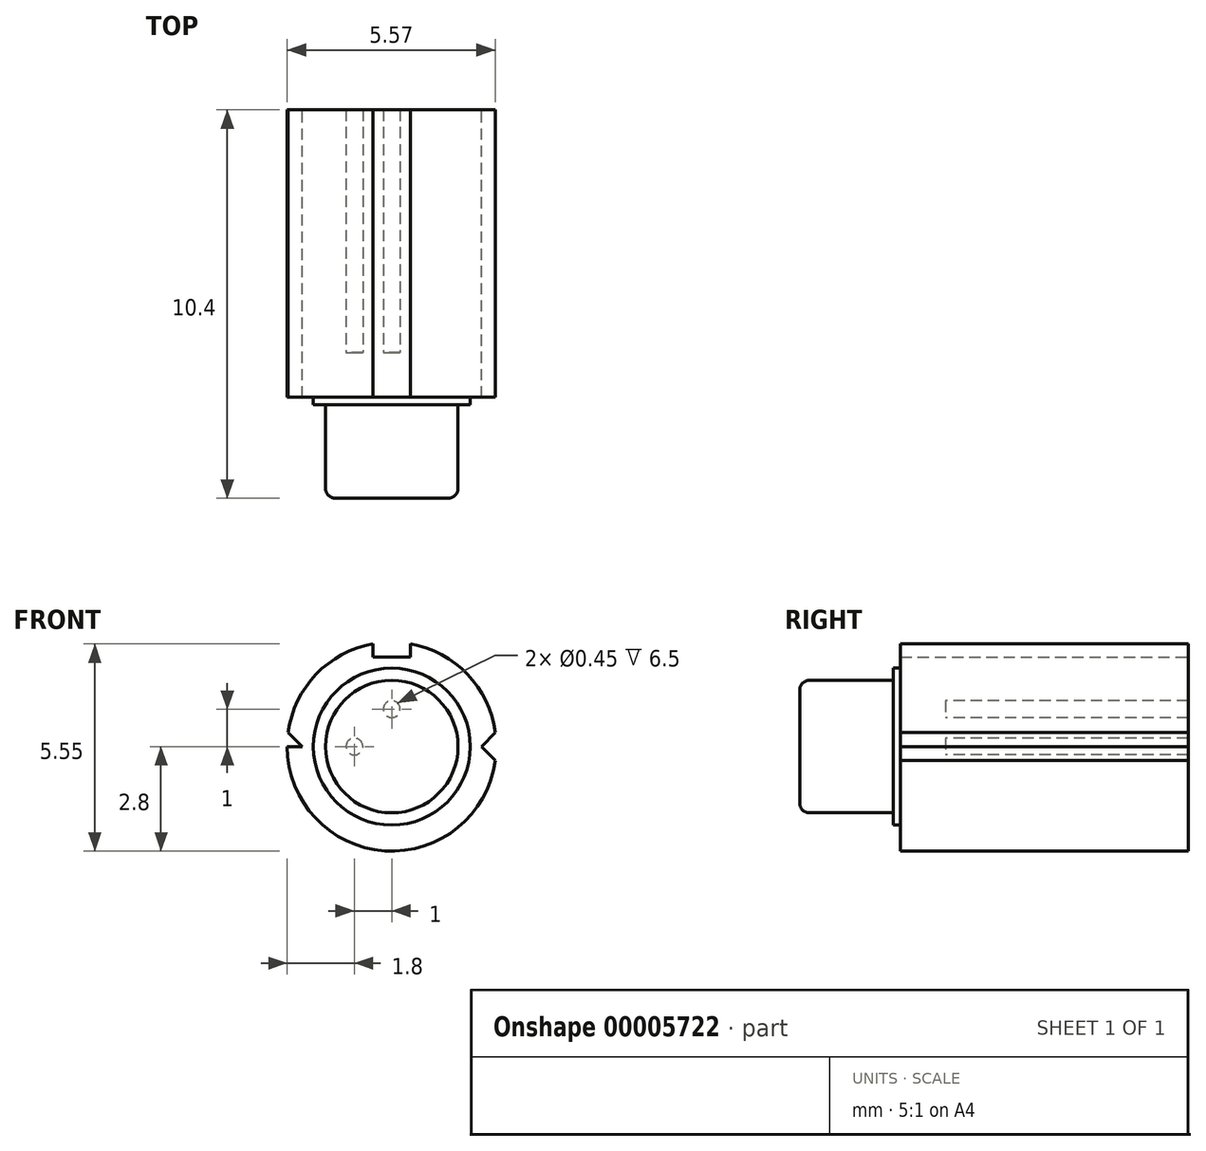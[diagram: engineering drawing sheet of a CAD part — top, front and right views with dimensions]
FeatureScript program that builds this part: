
annotation { "Feature Type Name" : "Feature", "Feature Type Description" : "" }
export const myFeature = defineFeature(function(context is Context, id is Id, definition is map)
    precondition{}
    {
        {
            var Q0;
            Q0=qCreatedBy(makeId("Front.planeOp"),FACE);
            var sketch = newSketch(context, id + "F0", { "sketchPlane" : qUnion([Q0])});
            skCircle(sketch, "E0", {"center": v(0, 0) * mm, "radius": 2.8 * mm});
            skSolve(sketch);
        }
        {
            var Q0;
            Q0=makeQuery(id+"F0.imprint","IMPRINT",FACE,{"disambiguationData":[TD([[makeQuery(id+"F0.imprint","IMPRINT",EDGE,{"derivedFrom":sQuery(id+"F0.wireOp",EDGE,"E0")}),1.0]])]});
            extrude(context, id + "F1", {"entities" : qUnion([Q0]), "depth" : 1.2 * mm});
        }
        {
            var Q0;
            Q0=makeQuery(id+"F1.opExtrude","CAP_FACE",FACE,{"disambiguationData":[OSD([sQuery(id+"F0.wireOp",EDGE,"E0")])],"isStart":false});
            var sketch = newSketch(context, id + "F2", { "sketchPlane" : qUnion([Q0])});
            skCircle(sketch, "E1", {"center": v(0, 0) * mm, "radius": 2.1 * mm});
            skSolve(sketch);
        }
        {
            var Q0;
            Q0=makeQuery(id+"F2.imprint","IMPRINT",FACE,{"disambiguationData":[TD([[makeQuery(id+"F2.imprint","IMPRINT",EDGE,{"derivedFrom":sQuery(id+"F2.wireOp",EDGE,"E1")}),1.0]])]});
            extrude(context, id + "F3", {"entities" : qUnion([Q0]), "operationType" : NewBodyOperationType.ADD, "depth" : 0.2 * mm});
        }
        {
            var Q0;
            Q0=makeQuery(id+"F3.opExtrude","CAP_FACE",FACE,{"disambiguationData":[OSD([sQuery(id+"F2.wireOp",EDGE,"E1")])],"isStart":false});
            var sketch = newSketch(context, id + "F4", { "sketchPlane" : qUnion([Q0])});
            skCircle(sketch, "E2", {"center": v(0, 0) * mm, "radius": 1.77 * mm});
            skSolve(sketch);
        }
        {
            var Q0;
            Q0=makeQuery(id+"F4.imprint","IMPRINT",FACE,{"disambiguationData":[TD([[makeQuery(id+"F4.imprint","IMPRINT",EDGE,{"derivedFrom":sQuery(id+"F4.wireOp",EDGE,"E2")}),1.0]])]});
            extrude(context, id + "F5", {"entities" : qUnion([Q0]), "operationType" : NewBodyOperationType.ADD, "depth" : 2.5 * mm});
        }
        {
            var Q0;
            Q0=makeQuery(id+"F5.opExtrude","CAP_EDGE",EDGE,{"disambiguationData":[OSD([sQuery(id+"F4.wireOp",EDGE,"E2")])],"isStart":false});
            fillet(context, id + "F6", {"entities" : qUnion([Q0]), "radius" : 0.27 * mm, "tangentPropagation" : true, "allowEdgeOverflow" : false});
        }
        {
            var Q0;
            Q0=makeQuery(id+"F1.opExtrude","CAP_FACE",FACE,{"disambiguationData":[OSD([sQuery(id+"F0.wireOp",EDGE,"E0")])],"isStart":true});
            var sketch = newSketch(context, id + "F7", { "sketchPlane" : qUnion([Q0])});
            skPoint(sketch, "E3", {"position": v(2.4, 0) * mm});
            skPoint(sketch, "E4", {"position": v(-2.4, 0) * mm});
            skLineSegment(sketch, "E5", {"start": v(2.4, 0) * mm, "end": v(2.77, -0.37) * mm});
            skLineSegment(sketch, "E6", {"start": v(2.77, -0.37) * mm, "end": v(2.4, 0) * mm});
            skLineSegment(sketch, "E7", {"start": v(2.4, 0) * mm, "end": v(2.77, 0.37) * mm});
            skLineSegment(sketch, "E8", {"start": v(2.8, 0) * mm, "end": v(-2.8, 0) * mm});
            skLineSegment(sketch, "E9", {"start": v(-2.4, 0) * mm, "end": v(-2.77, -0.37) * mm});
            skLineSegment(sketch, "E10", {"start": v(-2.4, 0) * mm, "end": v(-2.77, 0.37) * mm});
            skCircle(sketch, "E11", {"center": v(0, 0) * mm, "radius": 2.8 * mm});
            skPoint(sketch, "E12", {"position": v(0, 2.4) * mm});
            skLineSegment(sketch, "E13", {"start": v(0, 2.4) * mm, "end": v(0.5, 2.4) * mm});
            skLineSegment(sketch, "E14", {"start": v(0, 2.4) * mm, "end": v(-0.5, 2.4) * mm});
            skLineSegment(sketch, "E15", {"start": v(-0.5, 2.4) * mm, "end": v(-0.5, 2.75) * mm});
            skLineSegment(sketch, "E16", {"start": v(0.5, 2.4) * mm, "end": v(0.5, 2.75) * mm});
            skSolve(sketch);
        }
        {
            var Q0;
            {var subQ3=sQuery(id+"F7.wireOp",EDGE,"E7");Q0=makeQuery(id+"F7.imprint","IMPRINT",FACE,{"disambiguationData":[TD([[makeQuery(id+"F7.imprint","IMPRINT",EDGE,{"derivedFrom":subQ3}),-1.0]])]});}
            var Q1;
            {var subQ3=sQuery(id+"F7.wireOp",EDGE,"E6");Q1=makeQuery(id+"F7.imprint","IMPRINT",FACE,{"disambiguationData":[TD([[makeQuery(id+"F7.imprint","IMPRINT",EDGE,{"derivedFrom":subQ3}),-1.0]])]});}
            var Q2;
            {var subQ1=sQuery(id+"F7.wireOp",EDGE,"E9");Q2=makeQuery(id+"F7.imprint","IMPRINT",FACE,{"disambiguationData":[TD([[makeQuery(id+"F7.imprint","IMPRINT",EDGE,{"derivedFrom":subQ1}),-1.0]])]});}
            var Q3;
            {var subQ1=sQuery(id+"F7.wireOp",EDGE,"E10");Q3=makeQuery(id+"F7.imprint","IMPRINT",FACE,{"disambiguationData":[TD([[makeQuery(id+"F7.imprint","IMPRINT",EDGE,{"derivedFrom":subQ1}),1.0]])]});}
            var Q4;
            Q4=makeQuery(id+"F7.imprint","IMPRINT",FACE,{"disambiguationData":[TD([[makeQuery(id+"F7.imprint","IMPRINT",EDGE,{"derivedFrom":sQuery(id+"F7.wireOp",EDGE,"E13")}),1.0]])]});
            extrude(context, id + "F8", {"entities" : qUnion([Q0, Q1, Q2, Q3, Q4]), "operationType" : NewBodyOperationType.REMOVE, "endBound" : BoundingType.THROUGH_ALL, "oppositeDirection" : true, "depth" : 25 * mm});
        }
        {
            var Q0;
            Q0=makeQuery(id+"F1.opExtrude","CAP_FACE",FACE,{"disambiguationData":[OSD([sQuery(id+"F0.wireOp",EDGE,"E0")])],"isStart":true});
            var sketch = newSketch(context, id + "F9", { "sketchPlane" : qUnion([Q0])});
            skCircle(sketch, "E17", {"center": v(0, 0) * mm, "radius": 1 * mm});
            skPoint(sketch, "E18", {"position": v(0, 1) * mm});
            skPoint(sketch, "E19", {"position": v(-1, 0) * mm});
            skPoint(sketch, "E20", {"position": v(1, 0) * mm});
            skCircle(sketch, "E21", {"center": v(1, 0) * mm, "radius": 0.23 * mm});
            skCircle(sketch, "E22", {"center": v(0, 1) * mm, "radius": 0.23 * mm});
            skCircle(sketch, "E23", {"center": v(-1, 0) * mm, "radius": 0.23 * mm});
            skSolve(sketch);
        }
        {
            var Q0;
            {var subQ0=sQuery(id+"F9.wireOp",EDGE,"E22");var subQ1=sQuery(id+"F9.wireOp",EDGE,"E17");var subQ3=makeQuery(id+"F9.imprint","INTERSECT",VERTEX,{"disambiguationData":[OD(0.0)],"derivedFrom":[subQ1,subQ0]});Q0=makeQuery(id+"F9.imprint","IMPRINT",FACE,{"disambiguationData":[TD([[makeQuery(id+"F9.imprint","IMPRINT",EDGE,{"disambiguationData":[TD([[subQ3,-1.0]])],"derivedFrom":subQ1}),1.0]])]});}
            var Q1;
            {var subQ0=sQuery(id+"F9.wireOp",EDGE,"E22");var subQ1=sQuery(id+"F9.wireOp",EDGE,"E17");var subQ3=makeQuery(id+"F9.imprint","INTERSECT",VERTEX,{"disambiguationData":[OD(0.0)],"derivedFrom":[subQ1,subQ0]});Q1=makeQuery(id+"F9.imprint","IMPRINT",FACE,{"disambiguationData":[TD([[makeQuery(id+"F9.imprint","IMPRINT",EDGE,{"disambiguationData":[TD([[subQ3,-1.0]])],"derivedFrom":subQ1}),-1.0]])]});}
            var Q2;
            {var subQ0=sQuery(id+"F9.wireOp",EDGE,"E23");var subQ1=sQuery(id+"F9.wireOp",EDGE,"E17");var subQ3=makeQuery(id+"F9.imprint","INTERSECT",VERTEX,{"disambiguationData":[OD(0.0)],"derivedFrom":[subQ1,subQ0]});Q2=makeQuery(id+"F9.imprint","IMPRINT",FACE,{"disambiguationData":[TD([[makeQuery(id+"F9.imprint","IMPRINT",EDGE,{"disambiguationData":[TD([[subQ3,-1.0]])],"derivedFrom":subQ1}),1.0]])]});}
            var Q3;
            {var subQ0=sQuery(id+"F9.wireOp",EDGE,"E23");var subQ1=sQuery(id+"F9.wireOp",EDGE,"E17");var subQ3=makeQuery(id+"F9.imprint","INTERSECT",VERTEX,{"disambiguationData":[OD(0.0)],"derivedFrom":[subQ1,subQ0]});Q3=makeQuery(id+"F9.imprint","IMPRINT",FACE,{"disambiguationData":[TD([[makeQuery(id+"F9.imprint","IMPRINT",EDGE,{"disambiguationData":[TD([[subQ3,-1.0]])],"derivedFrom":subQ1}),-1.0]])]});}
            var Q4;
            {var subQ0=sQuery(id+"F9.wireOp",EDGE,"E21");var subQ1=sQuery(id+"F9.wireOp",EDGE,"E17");var subQ3=makeQuery(id+"F9.imprint","INTERSECT",VERTEX,{"disambiguationData":[OD(0.0)],"derivedFrom":[subQ1,subQ0]});Q4=makeQuery(id+"F9.imprint","IMPRINT",FACE,{"disambiguationData":[TD([[makeQuery(id+"F9.imprint","IMPRINT",EDGE,{"disambiguationData":[TD([[subQ3,1.0]])],"derivedFrom":subQ1}),1.0]])]});}
            var Q5;
            {var subQ0=sQuery(id+"F9.wireOp",EDGE,"E21");var subQ1=sQuery(id+"F9.wireOp",EDGE,"E17");var subQ3=makeQuery(id+"F9.imprint","INTERSECT",VERTEX,{"disambiguationData":[OD(0.0)],"derivedFrom":[subQ1,subQ0]});Q5=makeQuery(id+"F9.imprint","IMPRINT",FACE,{"disambiguationData":[TD([[makeQuery(id+"F9.imprint","IMPRINT",EDGE,{"disambiguationData":[TD([[subQ3,1.0]])],"derivedFrom":subQ1}),-1.0]])]});}
            extrude(context, id + "F10", {"entities" : qUnion([Q0, Q1, Q2, Q3, Q4, Q5]), "operationType" : NewBodyOperationType.ADD, "depth" : 6.5 * mm});
        }
    });
